# Revit family: 1Plumbing-Fixture_Mincey-Marble-Manufacturing_TP-Transfer-Shower-Pan
name_source: partatom
category: Plumbing Fixtures
units: mm (PartAtom-declared; Revit-internal decimal feet)

## family parameters
Cut with Voids When Loaded = No
Host = Face
Maintain Annotation Orientation = No
OmniClass Number = 23.45.05.14.11.21
Part Type = Normal
Room Calculation Point = No
Round Connector Dimension = Use Diameter
Shared = No

## types (2) — shared parameters
Assembly Code = D2010.60
Default Elevation = 48 "
Drain Diameter = 2 "
Drain Horizontal Offset = 19 "
Drain Vertical Offset = 19 "
Flow = 0 GPM
Height = 4 "
Keynote = 22 40 00.B5
Length = 38 "
Manufacturer = Mincey Marble Manufacturing
Product Documentation Link = https://minceymarble.com
Product Page URL = https://minceymarble.com
URL = https://minceymarble.com
Version = 1

## per-type parameters (varying)
| type | Depth | Description | Model |
| TP-3738 - Center Drain Transfer Shower Pan | 37 " | 37 x 38 Center Drain Transfer Shower Pan | TP-3738-C-SF |
| TP-3838 - Center Drain Transfer Shower Pan | 38 " | 38 x 38 Center Drain Transfer Shower Pan | TP-3838-C-SF |

## geometry (parser evidence)
native form markers: Sweep x3
no freeform markers — native parametric forms only
